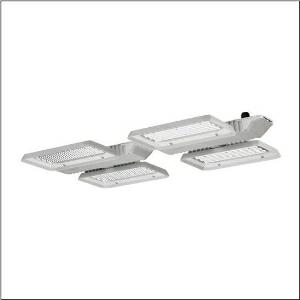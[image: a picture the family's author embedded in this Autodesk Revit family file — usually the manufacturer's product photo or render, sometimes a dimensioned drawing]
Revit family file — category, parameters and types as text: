
# Revit family: highbay_11_51hla2d24nca
name_source: partatom
category: Lighting Fixtures
units: mm (PartAtom-declared; Revit-internal decimal feet)

## family parameters
Cut with Voids When Loaded = No
Host = Face
Light Source = No
Part Type = Normal
Room Calculation Point = No
Round Connector Dimension = Use Diameter
Shared = No

## types (1)
- --- (1 x LED, 33150 lm, 189.6 W, 4000K)
    Apparent Load = 190 VA
    CIE Flux Codes = 89 96 99 100 100
    Color Rendering = 80
    Color Temperature = 4000K
    Default Elevation = 1800 mm
    Description = Highbay 11, LED high bay luminaire, primary light control with lens, of PMMA, light emission: direct distribution, primary light characteristic: symmetric, installation type: surface-mounted, suspended mounting, for 2x 2 x LED rated luminous flux: 33.150 lm, light colour: 840, colour temperature: 4000K, control gear: ECG DALI, with terminal, 5-pole, max. 2.5mm², mains connection: 230..240V, AC, 50/60Hz, rated input power: 190W, LED unit, of diecast aluminium, unplated, bead blasted, silver, length: 940 mm, width: 500 mm, height: 65mm, housing, of diecast aluminium, uncoated, bead blasted, silver, protection rating (complete): IP65, insulation class (complete): insulation class I (protective earthing), certification: CE, ENEC, VDE, protection symbol: D, impact resistance: IK08 with glass or PC cover, permissible ambient temperature for indoor applications: -35..+45°C, reducing of maximum allowable ambient temperature of 5°C with ceiling mounting, corresponds to IFS (International Featured Standards) requirements for safety and quality in the food industry, packaging unit: 1 piece
    Height = 95 mm
    Lamp = 1 x LED
    Lamp Light Flux = 33150 lm
    Lamp Power = 189.6 W
    Lamp count = 1
    Length = 939 mm
    Luminous efficacy = 175 lm/W
    Manufacturer = Siteco
    ModVariant = No
    Model = 51HLA2D24NCA
    Mounting Place = Ceiling
    Mounting Type = Pendant
    Number of Poles = 1
    OnlyDefault = Yes
    Power Factor = 1
    Product Name = Highbay 11
    Product group = LED high bay luminaire
    ProductGroupID = 903
    Protection Class = Protection class I
    Protection Degree = IP 65
    RLX_Detail_Level = 1
    RlxData = <blob elided: 96493 chars, md5=8435ac61>
    Socket = socket
    Standby Power = 0 W
    System Light Flux = 33150 lm
    System Power = 190 W
    Type Comments = factory setting: luminous flux: 100 % | dim-lin: 254 | 535 mA
    Type Image = l_1003428.jpg
    URL = http://relux.com
    VarID = @adj_140859
    Voltage = 0 V
    Weight = 0.00 kg
    Width = 501 mm

## geometry (parser evidence)
native form markers: Blend x4, Sweep x12
no freeform markers — native parametric forms only
